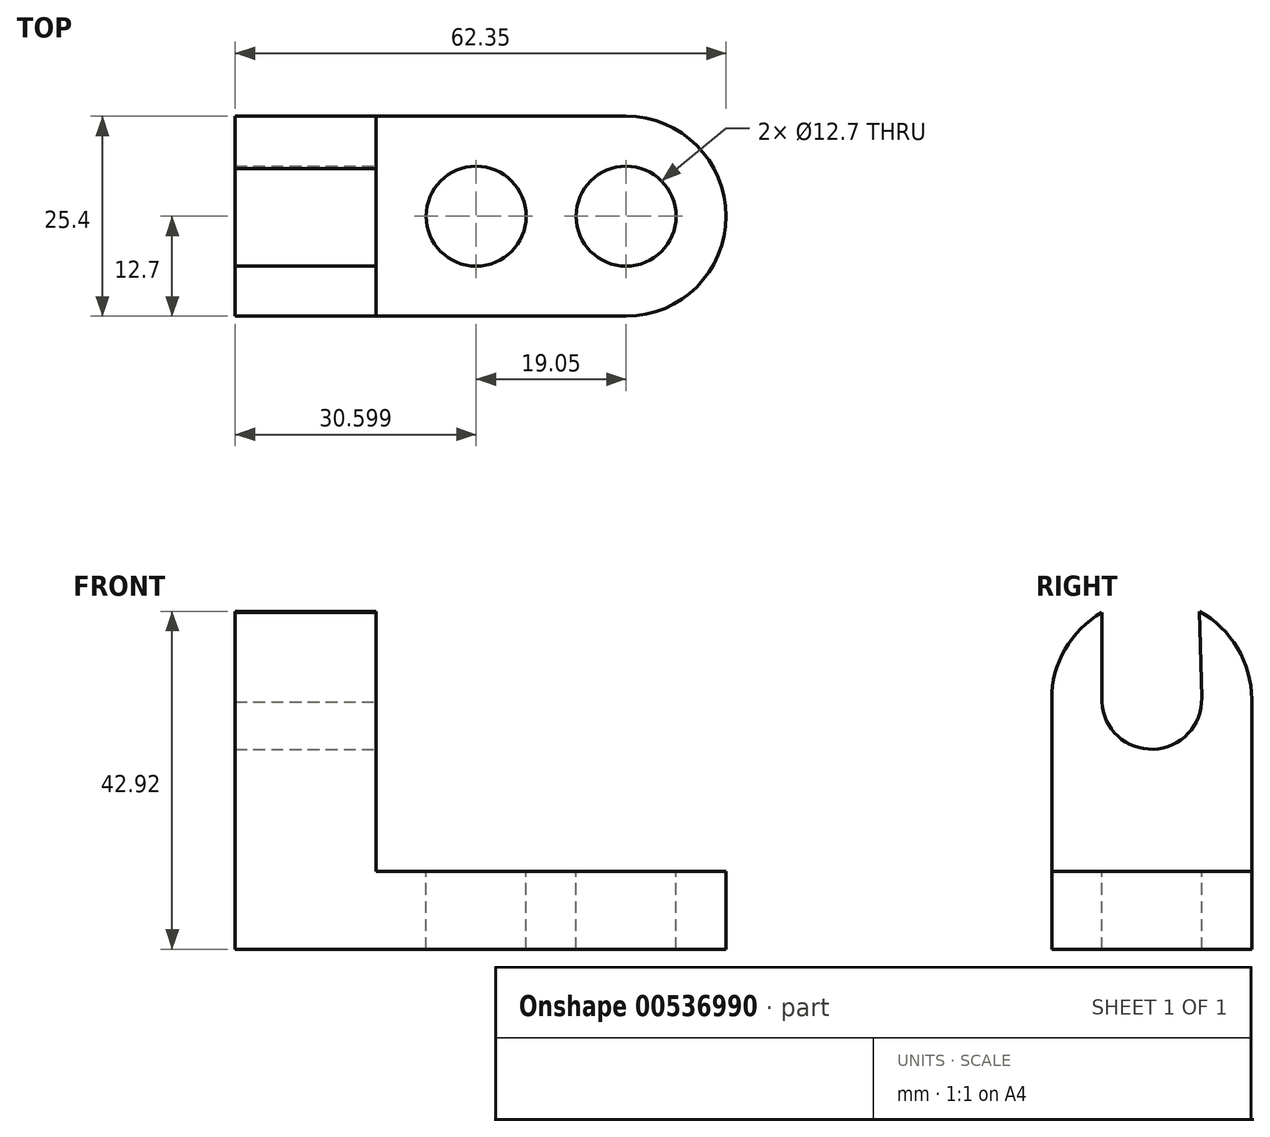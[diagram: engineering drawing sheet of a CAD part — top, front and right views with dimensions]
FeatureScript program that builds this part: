
annotation { "Feature Type Name" : "Feature", "Feature Type Description" : "" }
export const myFeature = defineFeature(function(context is Context, id is Id, definition is map)
    precondition{}
    {
        {
            var Q0;
            Q0=qCreatedBy(makeId("Front.planeOp"),FACE);
            var sketch = newSketch(context, id + "F0", { "sketchPlane" : qUnion([Q0])});
            skLineSegment(sketch, "E0", {"start": v(-72.17, 13.5) * mm, "end": v(-9.82, 13.5) * mm});
            skLineSegment(sketch, "E1", {"start": v(-9.82, 13.5) * mm, "end": v(-9.82, 23.38) * mm});
            skLineSegment(sketch, "E2", {"start": v(-9.82, 23.38) * mm, "end": v(-54.27, 23.38) * mm});
            skLineSegment(sketch, "E3", {"start": v(-54.27, 23.38) * mm, "end": v(-54.27, 57.95) * mm});
            skLineSegment(sketch, "E4", {"start": v(-72.17, 13.5) * mm, "end": v(-72.17, 57.95) * mm});
            skLineSegment(sketch, "E5", {"start": v(-72.17, 57.95) * mm, "end": v(-54.27, 57.95) * mm});
            skSolve(sketch);
        }
        {
            var Q0;
            Q0=makeQuery(id+"F0.imprint","IMPRINT",FACE,{"disambiguationData":[TD([[makeQuery(id+"F0.imprint","IMPRINT",EDGE,{"derivedFrom":sQuery(id+"F0.wireOp",EDGE,"E0")}),1.0]])]});
            extrude(context, id + "F1", {"entities" : qUnion([Q0]), "depth" : 25.4 * mm, "offsetDistance" : 25.4 * mm});
        }
        {
            var Q0;
            Q0=makeQuery(id+"F1.opExtrude","SWEPT_FACE",FACE,{"disambiguationData":[OSD([sQuery(id+"F0.wireOp",EDGE,"E2")])]});
            var sketch = newSketch(context, id + "F2", { "sketchPlane" : qUnion([Q0])});
            skLineSegment(sketch, "E6", {"start": v(-9.82, 0) * mm, "end": v(-22.52, 0) * mm});
            skLineSegment(sketch, "E7", {"start": v(-9.82, -25.4) * mm, "end": v(-22.52, -25.4) * mm});
            skArc(sketch, "E8", {"start": v(-22.52, -25.4) * mm, "mid": v(-9.82, -12.7) * mm, "end": v(-22.52, 0) * mm});
            skSolve(sketch);
        }
        {
            var Q0;
            {var subQ0=sQuery(id+"F2.wireOp",EDGE,"E6");Q0=makeQuery(id+"F2.imprint","IMPRINT",FACE,{"disambiguationData":[TD([[makeQuery(id+"F2.imprint","IMPRINT",EDGE,{"derivedFrom":subQ0}),1.0]])]});}
            var Q1;
            {var subQ0=sQuery(id+"F2.wireOp",EDGE,"E7");Q1=makeQuery(id+"F2.imprint","IMPRINT",FACE,{"disambiguationData":[TD([[makeQuery(id+"F2.imprint","IMPRINT",EDGE,{"derivedFrom":subQ0}),-1.0]])]});}
            extrude(context, id + "F3", {"entities" : qUnion([Q0, Q1]), "operationType" : NewBodyOperationType.REMOVE, "endBound" : BoundingType.THROUGH_ALL, "oppositeDirection" : true, "depth" : 25.4 * mm, "offsetDistance" : 25.4 * mm});
        }
        {
            var Q0;
            Q0=makeQuery(id+"F1.opExtrude","SWEPT_FACE",FACE,{"disambiguationData":[OSD([sQuery(id+"F0.wireOp",EDGE,"E3")])]});
            var sketch = newSketch(context, id + "F4", { "sketchPlane" : qUnion([Q0])});
            skLineSegment(sketch, "E9", {"start": v(-25.4, 57.95) * mm, "end": v(-25.4, 45.25) * mm});
            skLineSegment(sketch, "E10", {"start": v(0, 57.95) * mm, "end": v(0, 45.25) * mm});
            skArc(sketch, "E11", {"start": v(0, 45.25) * mm, "mid": v(-12.7, 57.95) * mm, "end": v(-25.4, 45.25) * mm});
            skSolve(sketch);
        }
        {
            var Q0;
            {var subQ0=sQuery(id+"F4.wireOp",EDGE,"E9");Q0=makeQuery(id+"F4.imprint","IMPRINT",FACE,{"disambiguationData":[TD([[makeQuery(id+"F4.imprint","IMPRINT",EDGE,{"derivedFrom":subQ0}),-1.0]])]});}
            var Q1;
            {var subQ0=sQuery(id+"F4.wireOp",EDGE,"E10");Q1=makeQuery(id+"F4.imprint","IMPRINT",FACE,{"disambiguationData":[TD([[makeQuery(id+"F4.imprint","IMPRINT",EDGE,{"derivedFrom":subQ0}),1.0]])]});}
            extrude(context, id + "F5", {"entities" : qUnion([Q0, Q1]), "operationType" : NewBodyOperationType.REMOVE, "endBound" : BoundingType.THROUGH_ALL, "oppositeDirection" : true, "depth" : 25.4 * mm, "offsetDistance" : 25.4 * mm});
        }
        {
            var Q0;
            Q0=makeQuery(id+"F1.opExtrude","SWEPT_FACE",FACE,{"disambiguationData":[OSD([sQuery(id+"F0.wireOp",EDGE,"E3")])]});
            var sketch = newSketch(context, id + "F6", { "sketchPlane" : qUnion([Q0])});
            skCircle(sketch, "E12", {"center": v(-12.7, 45.25) * mm, "radius": 6.35 * mm});
            skLineSegment(sketch, "E13", {"start": v(-19.04, 44.94) * mm, "end": v(-19.04, 56.26) * mm});
            skLineSegment(sketch, "E14", {"start": v(-6.35, 45.42) * mm, "end": v(-6.64, 56.42) * mm});
            skSolve(sketch);
        }
        {
            var Q0;
            {var subQ0=sQuery(id+"F6.wireOp",EDGE,"E14");Q0=makeQuery(id+"F6.imprint","IMPRINT",FACE,{"disambiguationData":[TD([[makeQuery(id+"F6.imprint","IMPRINT",EDGE,{"derivedFrom":subQ0}),1.0]])]});}
            var Q1;
            {var subQ0=sQuery(id+"F6.wireOp",EDGE,"E12");var subQ1=makeQuery(id+"F6.imprint","INTERSECT",VERTEX,{"derivedFrom":[subQ0,sQuery(id+"F6.wireOp",EDGE,"E14")]});Q1=makeQuery(id+"F6.imprint","IMPRINT",FACE,{"disambiguationData":[TD([[makeQuery(id+"F6.imprint","IMPRINT",EDGE,{"disambiguationData":[TD([[subQ1,-1.0]])],"derivedFrom":subQ0}),1.0]])]});}
            extrude(context, id + "F7", {"entities" : qUnion([Q0, Q1]), "operationType" : NewBodyOperationType.REMOVE, "endBound" : BoundingType.THROUGH_ALL, "oppositeDirection" : true, "depth" : 25.4 * mm, "offsetDistance" : 25.4 * mm});
        }
        {
            var Q0;
            Q0=makeQuery(id+"F1.opExtrude","SWEPT_FACE",FACE,{"disambiguationData":[OSD([sQuery(id+"F0.wireOp",EDGE,"E2")])]});
            var sketch = newSketch(context, id + "F8", { "sketchPlane" : qUnion([Q0])});
            skCircle(sketch, "E15", {"center": v(-22.52, -12.7) * mm, "radius": 6.35 * mm});
            skCircle(sketch, "E16", {"center": v(-41.57, -12.7) * mm, "radius": 6.35 * mm});
            skSolve(sketch);
        }
        {
            var Q0;
            Q0=makeQuery(id+"F8.imprint","IMPRINT",FACE,{"disambiguationData":[TD([[makeQuery(id+"F8.imprint","IMPRINT",EDGE,{"derivedFrom":sQuery(id+"F8.wireOp",EDGE,"E16")}),1.0]])]});
            var Q1;
            Q1=makeQuery(id+"F8.imprint","IMPRINT",FACE,{"disambiguationData":[TD([[makeQuery(id+"F8.imprint","IMPRINT",EDGE,{"derivedFrom":sQuery(id+"F8.wireOp",EDGE,"E15")}),1.0]])]});
            extrude(context, id + "F9", {"entities" : qUnion([Q0, Q1]), "operationType" : NewBodyOperationType.REMOVE, "endBound" : BoundingType.THROUGH_ALL, "oppositeDirection" : true, "depth" : 25.4 * mm, "offsetDistance" : 25.4 * mm});
        }
    });
